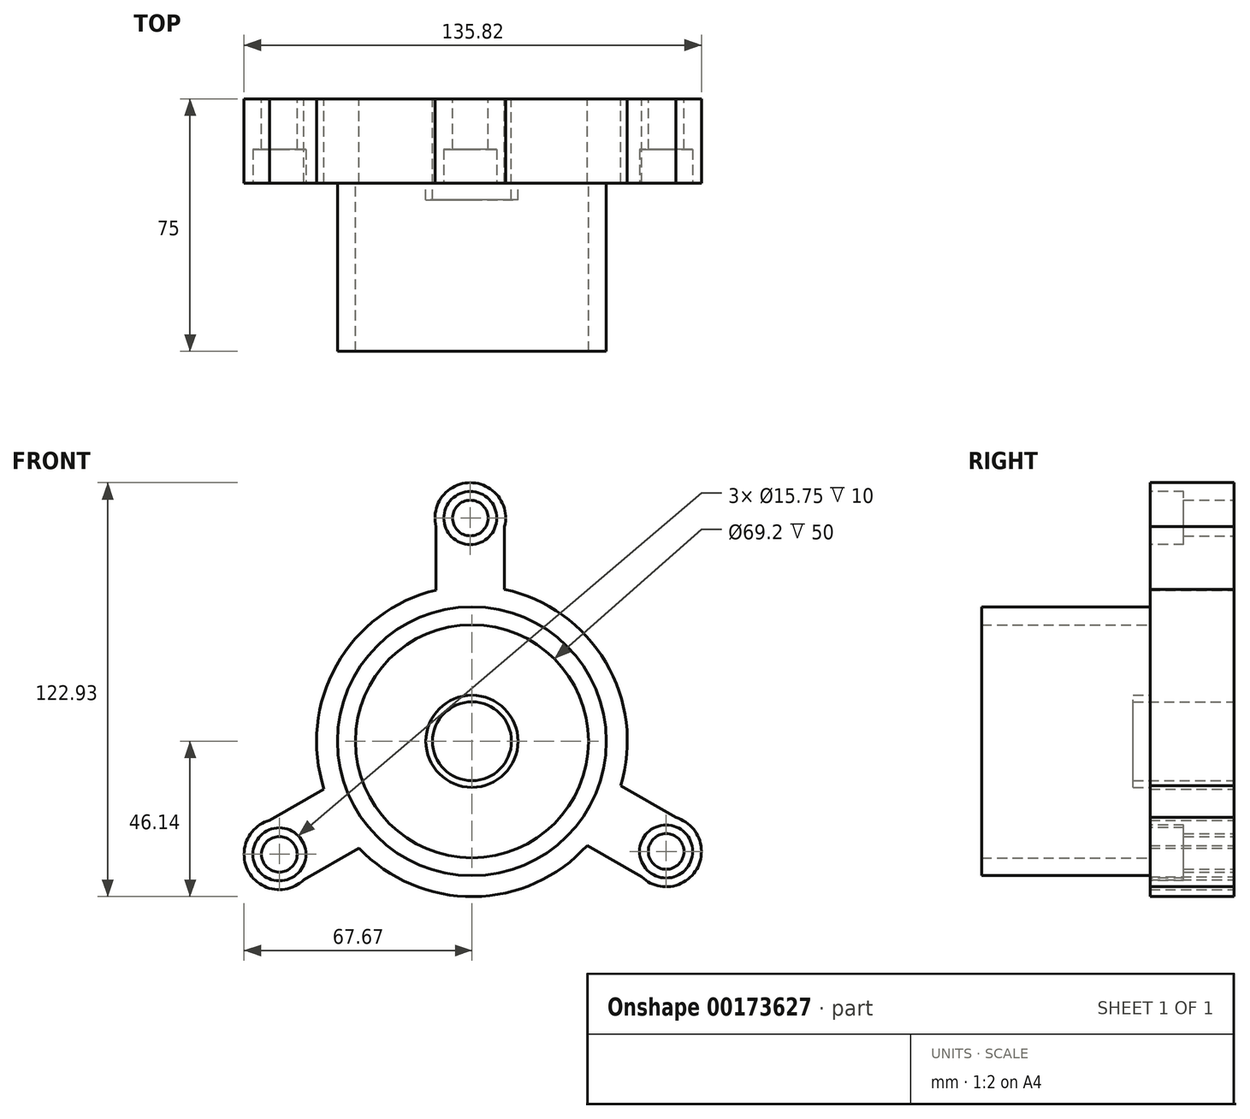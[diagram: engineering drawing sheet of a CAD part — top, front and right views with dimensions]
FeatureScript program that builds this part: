
annotation { "Feature Type Name" : "Feature", "Feature Type Description" : "" }
export const myFeature = defineFeature(function(context is Context, id is Id, definition is map)
    precondition{}
    {
        {
            var Q0;
            Q0=qCreatedBy(makeId("Front.planeOp"),FACE);
            var sketch = newSketch(context, id + "F0", { "sketchPlane" : qUnion([Q0])});
            skArc(sketch, "E0", {"start": v(-10.66, 44.9) * mm, "mid": v(-40.2, 22.64) * mm, "end": v(-43.92, -14.16) * mm});
            skLineSegment(sketch, "E1", {"start": v(-10.66, 44.9) * mm, "end": v(-10.66, 63.76) * mm});
            skLineSegment(sketch, "E2", {"start": v(9.7, 63.76) * mm, "end": v(9.7, 45.11) * mm});
            skArc(sketch, "E3", {"start": v(9.7, 63.76) * mm, "mid": v(-0.48, 76.79) * mm, "end": v(-10.66, 63.76) * mm});
            skCircle(sketch, "E4", {"center": v(-0.48, 66.3) * mm, "radius": 5.29 * mm});
            skCircle(sketch, "E5.1.0", {"center": v(-57.17, -33.57) * mm, "radius": 5.29 * mm});
            skArc(sketch, "E5.1.1", {"start": v(-60.07, -23.48) * mm, "mid": v(-66.26, -38.81) * mm, "end": v(-49.89, -41.12) * mm});
            skLineSegment(sketch, "E5.1.2", {"start": v(-60.07, -23.48) * mm, "end": v(-43.92, -14.16) * mm});
            skLineSegment(sketch, "E5.1.3", {"start": v(-33.55, -31.68) * mm, "end": v(-49.89, -41.12) * mm});
            skCircle(sketch, "E5.2.0", {"center": v(57.66, -32.73) * mm, "radius": 5.29 * mm});
            skArc(sketch, "E5.2.1", {"start": v(50.37, -40.28) * mm, "mid": v(66.74, -37.98) * mm, "end": v(60.55, -22.65) * mm});
            skLineSegment(sketch, "E5.2.2", {"start": v(50.37, -40.28) * mm, "end": v(34.22, -30.95) * mm});
            skLineSegment(sketch, "E5.2.3", {"start": v(44.21, -13.21) * mm, "end": v(60.55, -22.65) * mm});
            skArc(sketch, "E6.trimOffspring", {"start": v(-33.55, -31.68) * mm, "mid": v(0.5, -46.14) * mm, "end": v(34.22, -30.95) * mm});
            skArc(sketch, "E7.trimOffspring", {"start": v(44.21, -13.21) * mm, "mid": v(39.71, 23.5) * mm, "end": v(9.7, 45.11) * mm});
            skSolve(sketch);
        }
        {
            var Q0;
            Q0=makeQuery(id+"F0.imprint","IMPRINT",FACE,{"disambiguationData":[TD([[makeQuery(id+"F0.imprint","IMPRINT",EDGE,{"derivedFrom":sQuery(id+"F0.wireOp",EDGE,"E0")}),1.0]])]});
            extrude(context, id + "F1", {"entities" : qUnion([Q0]), "depth" : 25 * mm});
        }
        {
            var Q0;
            Q0=qCreatedBy(makeId("Front.planeOp"),FACE);
            var sketch = newSketch(context, id + "F2", { "sketchPlane" : qUnion([Q0])});
            skCircle(sketch, "E8", {"center": v(0, 0) * mm, "radius": 39.92 * mm});
            skCircle(sketch, "E9", {"center": v(0, 0) * mm, "radius": 34.6 * mm});
            skSolve(sketch);
        }
        {
            var Q0;
            Q0 = qSketchRegion(id + "F2", true);
            extrude(context, id + "F3", {"entities" : qUnion([Q0]), "operationType" : NewBodyOperationType.ADD, "depth" : 75 * mm});
        }
        {
            var Q0;
            Q0=qCreatedBy(makeId("Front.planeOp"),FACE);
            var sketch = newSketch(context, id + "F4", { "sketchPlane" : qUnion([Q0])});
            skCircle(sketch, "E10", {"center": v(0, 0) * mm, "radius": 11.72 * mm});
            skSolve(sketch);
        }
        {
            var Q0;
            Q0=makeQuery(id+"F4.imprint","IMPRINT",FACE,{"disambiguationData":[TD([[makeQuery(id+"F4.imprint","IMPRINT",EDGE,{"derivedFrom":sQuery(id+"F4.wireOp",EDGE,"E10")}),1.0]])]});
            var Q1;
            Q1=sQuery(id+"F4.wireOp",EDGE,"E10");
            extrude(context, id + "F5", {"entities" : qUnion([Q0]), "operationType" : NewBodyOperationType.REMOVE, "surfaceEntities" : qUnion([Q1]), "depth" : 25 * mm});
        }
        {
            var Q0;
            {var subQ0=sQuery(id+"F0.wireOp",EDGE,"E5.2.0");var subQ1=sQuery(id+"F0.wireOp",EDGE,"E5.1.2");var subQ2=sQuery(id+"F0.wireOp",EDGE,"E7.trimOffspring");var subQ3=sQuery(id+"F0.wireOp",EDGE,"E5.1.1");var subQ4=sQuery(id+"F0.wireOp",EDGE,"E5.1.0");var subQ5=sQuery(id+"F0.wireOp",EDGE,"E4");var subQ6=sQuery(id+"F0.wireOp",EDGE,"E0");var subQ7=sQuery(id+"F0.wireOp",EDGE,"E5.1.3");var subQ8=sQuery(id+"F0.wireOp",EDGE,"E1");var subQ9=sQuery(id+"F0.wireOp",EDGE,"E2");var subQ10=sQuery(id+"F0.wireOp",EDGE,"E3");var subQ11=sQuery(id+"F0.wireOp",EDGE,"E5.2.1");var subQ12=sQuery(id+"F0.wireOp",EDGE,"E5.2.2");var subQ13=sQuery(id+"F0.wireOp",EDGE,"E5.2.3");var subQ14=sQuery(id+"F0.wireOp",EDGE,"E6.trimOffspring");Q0=makeQuery(id+"F3.boolean.opBoolean","SPLIT",FACE,{"disambiguationData":[TD([makeQuery(id+"F1.opExtrude","SWEPT_FACE",FACE,{"disambiguationData":[OSD([subQ6])]})])],"derivedFrom":makeQuery(id+"F1.opExtrude","CAP_FACE",FACE,{"disambiguationData":[OSD([subQ6,subQ8,subQ9,subQ10,subQ5,subQ4,subQ3,subQ1,subQ7,subQ0,subQ11,subQ12,subQ13,subQ14,subQ2])],"isStart":false})});}
            var sketch = newSketch(context, id + "F6", { "sketchPlane" : qUnion([Q0])});
            skCircle(sketch, "E11", {"center": v(-0.48, 66.3) * mm, "radius": 7.87 * mm});
            skCircle(sketch, "E12.1.0", {"center": v(-57.17, -33.57) * mm, "radius": 7.87 * mm});
            skCircle(sketch, "E12.2.0", {"center": v(57.66, -32.73) * mm, "radius": 7.87 * mm});
            skPoint(sketch, "E12.center", {"position": v(0, 0) * mm});
            skSolve(sketch);
        }
        {
            var Q0;
            Q0=makeQuery(id+"F6.imprint","IMPRINT",FACE,{"disambiguationData":[TD([[makeQuery(id+"F6.imprint","IMPRINT",EDGE,{"derivedFrom":sQuery(id+"F6.wireOp",EDGE,"E11")}),1.0]])]});
            var Q1;
            Q1=makeQuery(id+"F6.imprint","IMPRINT",FACE,{"disambiguationData":[TD([[makeQuery(id+"F6.imprint","IMPRINT",EDGE,{"derivedFrom":sQuery(id+"F6.wireOp",EDGE,"E12.1.0")}),1.0]])]});
            var Q2;
            Q2=makeQuery(id+"F6.imprint","IMPRINT",FACE,{"disambiguationData":[TD([[makeQuery(id+"F6.imprint","IMPRINT",EDGE,{"derivedFrom":sQuery(id+"F6.wireOp",EDGE,"E12.2.0")}),1.0]])]});
            var Q3;
            Q3=sQuery(id+"F6.wireOp",EDGE,"E11");
            var Q4;
            Q4=sQuery(id+"F6.wireOp",EDGE,"E12.1.0");
            var Q5;
            Q5=sQuery(id+"F6.wireOp",EDGE,"E12.2.0");
            extrude(context, id + "F7", {"entities" : qUnion([Q0, Q1, Q2]), "operationType" : NewBodyOperationType.REMOVE, "surfaceEntities" : qUnion([Q3, Q4, Q5]), "oppositeDirection" : true, "depth" : 10 * mm});
        }
        {
            var Q0;
            Q0=makeQuery(id+"F3.boolean.opBoolean","SPLIT",FACE,{"disambiguationData":[TD([makeQuery(id+"F3.opExtrude","SWEPT_FACE",FACE,{"disambiguationData":[OSD([sQuery(id+"F2.wireOp",EDGE,"E9")])]})])],"derivedFrom":makeQuery(id+"F1.opExtrude","CAP_FACE",FACE,{"disambiguationData":[OSD([sQuery(id+"F0.wireOp",EDGE,"E0"),sQuery(id+"F0.wireOp",EDGE,"E1"),sQuery(id+"F0.wireOp",EDGE,"E2"),sQuery(id+"F0.wireOp",EDGE,"E3"),sQuery(id+"F0.wireOp",EDGE,"E4"),sQuery(id+"F0.wireOp",EDGE,"E5.1.0"),sQuery(id+"F0.wireOp",EDGE,"E5.1.1"),sQuery(id+"F0.wireOp",EDGE,"E5.1.2"),sQuery(id+"F0.wireOp",EDGE,"E5.1.3"),sQuery(id+"F0.wireOp",EDGE,"E5.2.0"),sQuery(id+"F0.wireOp",EDGE,"E5.2.1"),sQuery(id+"F0.wireOp",EDGE,"E5.2.2"),sQuery(id+"F0.wireOp",EDGE,"E5.2.3"),sQuery(id+"F0.wireOp",EDGE,"E6.trimOffspring"),sQuery(id+"F0.wireOp",EDGE,"E7.trimOffspring")])],"isStart":false})});
            var sketch = newSketch(context, id + "F8", { "sketchPlane" : qUnion([Q0])});
            skCircle(sketch, "E13", {"center": v(0, 0) * mm, "radius": 13.68 * mm});
            skSolve(sketch);
        }
        {
            var Q0;
            Q0=makeQuery(id+"F8.imprint","IMPRINT",FACE,{"disambiguationData":[TD([[makeQuery(id+"F8.imprint","IMPRINT",EDGE,{"derivedFrom":sQuery(id+"F8.wireOp",EDGE,"E13")}),1.0]])]});
            var Q1;
            Q1=sQuery(id+"F8.wireOp",EDGE,"E13");
            extrude(context, id + "F9", {"entities" : qUnion([Q0]), "operationType" : NewBodyOperationType.ADD, "surfaceEntities" : qUnion([Q1]), "depth" : 5 * mm});
        }
    });
